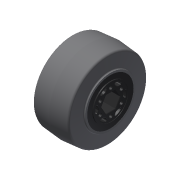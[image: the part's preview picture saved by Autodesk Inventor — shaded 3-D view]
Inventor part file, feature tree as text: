
AUTODESK INVENTOR PART (.ipt)
format: ipt  version: 2015 (Build 190159000, 159)  size: 1,773,568 bytes
history: native  units: in
note: dims shown in document units (in); Inventor stores cm internally (conversion verified against a paired STEP export)
features: revolve x1, other x1, extrude x1, mirror x1, imported_body x1, sketch x1
ambient origin geometry x8: Origin, YZ Plane, XZ Plane, XY Plane, X Axis, Y Axis, Z Axis, Center Point
bodies: Body1 (feature_tree)
feature tree (6):
  revolve  "Revolve1"  [1 undecoded]
  other  "217-4046-STEP-201410301"
  extrude  "Extrusion1"  [1 undecoded]
  mirror  "Mirror1"
  imported_body  "Base1"
  sketch  "Sketch1"  dims[d0=0.0039in d1=0.0in d2=1.4173in]
note: 2 required parameter values undecoded (feature->parameter linkage not recoverable at this tier; creation-order binding heuristic only, values carry confidence <= 0.55)